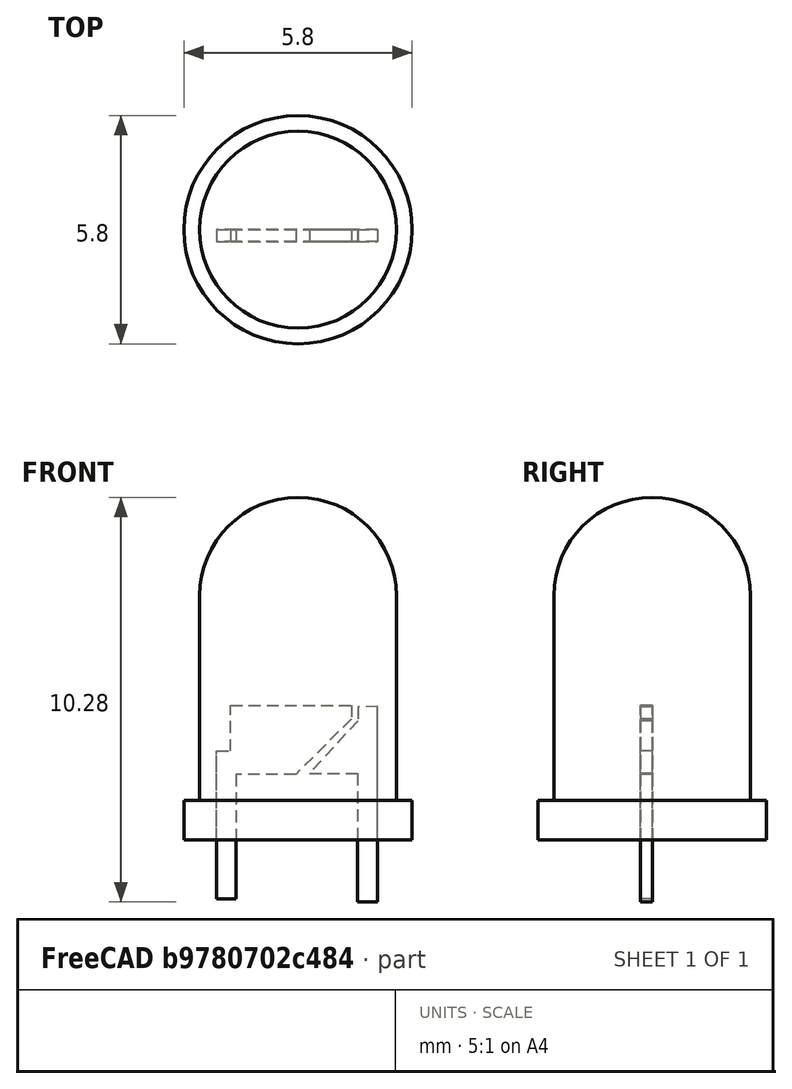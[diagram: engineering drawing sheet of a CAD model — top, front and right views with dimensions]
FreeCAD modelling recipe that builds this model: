
FCSTD DOCUMENT  (FreeCAD 0.14R3692 (Git))
Label: Led
License: CC-BY 3.0
LicenseURL: http://creativecommons.org/licenses/by/3.0/
objects: Part::Cylinder×2, Sketcher::SketchObject×2, PartDesign::Pad×2, Part::Sphere×1, Part::MultiFuse×1
note: 10 computed .brp shape members not serialized (recipe doc carries the construction recipe); baked Part::Feature solids carry a one-line shape summary decoded from their .brp

FEATURE [Part::Cylinder] Cylinder  label="Cilindro"
  Angle = 360
  Height = 6.2
  Radius = 2.5
FEATURE [Part::Sphere] Sphere  label="Esféra"
  Angle1 = -90
  Angle2 = 90
  Angle3 = 180
  Placement = pos=(0,0,6.2) rot=(1,0,0;1.5708rad)
  Radius = 2.5
FEATURE [Part::Cylinder] Cylinder001  label="Cilindro001"
  Angle = 360
  Height = 1
  Radius = 2.9
FEATURE [Part::MultiFuse] Fusion  label="Funda"
  Shapes = -> [Cylinder,Cylinder001,Sphere]
FEATURE [Sketcher::SketchObject] Sketch
  Placement = pos=(0,0,0) rot=(1,0,0;1.5708rad)
  sketch-geometry (9):
    g0: LineSegment StartX=-2.06901 StartY=-1.50757 StartZ=0 EndX=-2.06901 EndY=2.25482 EndZ=0
    g1: LineSegment StartX=-2.06901 StartY=2.25482 StartZ=0 EndX=-1.71216 EndY=2.25482 EndZ=0
    g2: LineSegment StartX=-1.71216 StartY=2.25482 StartZ=0 EndX=-1.71216 EndY=3.41819 EndZ=0
    g3: LineSegment StartX=-1.71216 StartY=3.41819 StartZ=0 EndX=1.35716 EndY=3.41819 EndZ=0
    g4: LineSegment StartX=1.35716 StartY=3.41819 StartZ=0 EndX=1.35716 EndY=3.07166 EndZ=0
    g5: LineSegment StartX=1.35716 StartY=3.07166 StartZ=0 EndX=-0.05374 EndY=1.66076 EndZ=0
    g6: LineSegment StartX=-0.05374 StartY=1.66076 StartZ=0 EndX=-1.56901 EndY=1.66076 EndZ=0
    g7: LineSegment StartX=-1.56901 StartY=1.66076 StartZ=0 EndX=-1.56901 EndY=-1.5 EndZ=0
    g8: LineSegment StartX=-1.56901 StartY=-1.5 StartZ=0 EndX=-2.06901 EndY=-1.50757 EndZ=0
  constraints (18):
    c: Vertical(g0)
    c: Coincident(g0,g1)
    c: Horizontal(g1)
    c: Coincident(g1,g2)
    c: Vertical(g2)
    c: Coincident(g2,g3)
    c: Horizontal(g3)
    c: Coincident(g3,g4)
    c: Vertical(g4)
    c: Coincident(g4,g5)
    c: Coincident(g5,g6)
    c: Horizontal(g6)
    c: Coincident(g6,g7)
    c: Vertical(g7)
    c: Coincident(g7,g8)
    c: Coincident(g8,g0)
    c: DistanceY(g-1,g7) = -1.5
    c: DistanceX(g0,g7) = 0.5
FEATURE [PartDesign::Pad] Pad  label="Catodo"
  Length = 0.3
  Length2 = 100
  Placement = pos=(0,0,0) rot=(1,0,0;1.5708rad)
  Sketch = -> Sketch
  Type = 0
FEATURE [Sketcher::SketchObject] Sketch001
  Placement = pos=(0,0,0) rot=(1,0,0;1.5708rad)
  sketch-geometry (7):
    g0: LineSegment StartX=2.0234 StartY=-1.57582 StartZ=0 EndX=2.0234 EndY=3.38927 EndZ=0
    g1: LineSegment StartX=2.0234 StartY=3.38927 StartZ=0 EndX=1.5234 EndY=3.36901 EndZ=0
    g2: LineSegment StartX=1.5234 StartY=3.36901 StartZ=0 EndX=1.5234 EndY=3.02449 EndZ=0
    g3: LineSegment StartX=1.5234 StartY=3.02449 StartZ=0 EndX=0.294592 EndY=1.68695 EndZ=0
    g4: LineSegment StartX=0.294592 StartY=1.68695 StartZ=0 EndX=1.51053 EndY=1.68695 EndZ=0
    g5: LineSegment StartX=1.51053 StartY=1.68695 StartZ=0 EndX=1.51053 EndY=-1.57582 EndZ=0
    g6: LineSegment StartX=1.51053 StartY=-1.57582 StartZ=0 EndX=2.0234 EndY=-1.57582 EndZ=0
  constraints (13):
    c: Vertical(g0)
    c: Coincident(g1,g0)
    c: DistanceX(g1,g0) = 0.5
    c: Coincident(g1,g2)
    c: Vertical(g2)
    c: Coincident(g2,g3)
    c: Coincident(g3,g4)
    c: Horizontal(g4)
    c: Coincident(g4,g5)
    c: Vertical(g5)
    c: Coincident(g5,g6)
    c: Coincident(g6,g0)
    c: Horizontal(g6)
FEATURE [PartDesign::Pad] Pad001  label="Anodo"
  Length = 0.3
  Length2 = 100
  Placement = pos=(0,0,0) rot=(1,0,0;1.5708rad)
  Sketch = -> Sketch001
  Type = 0
